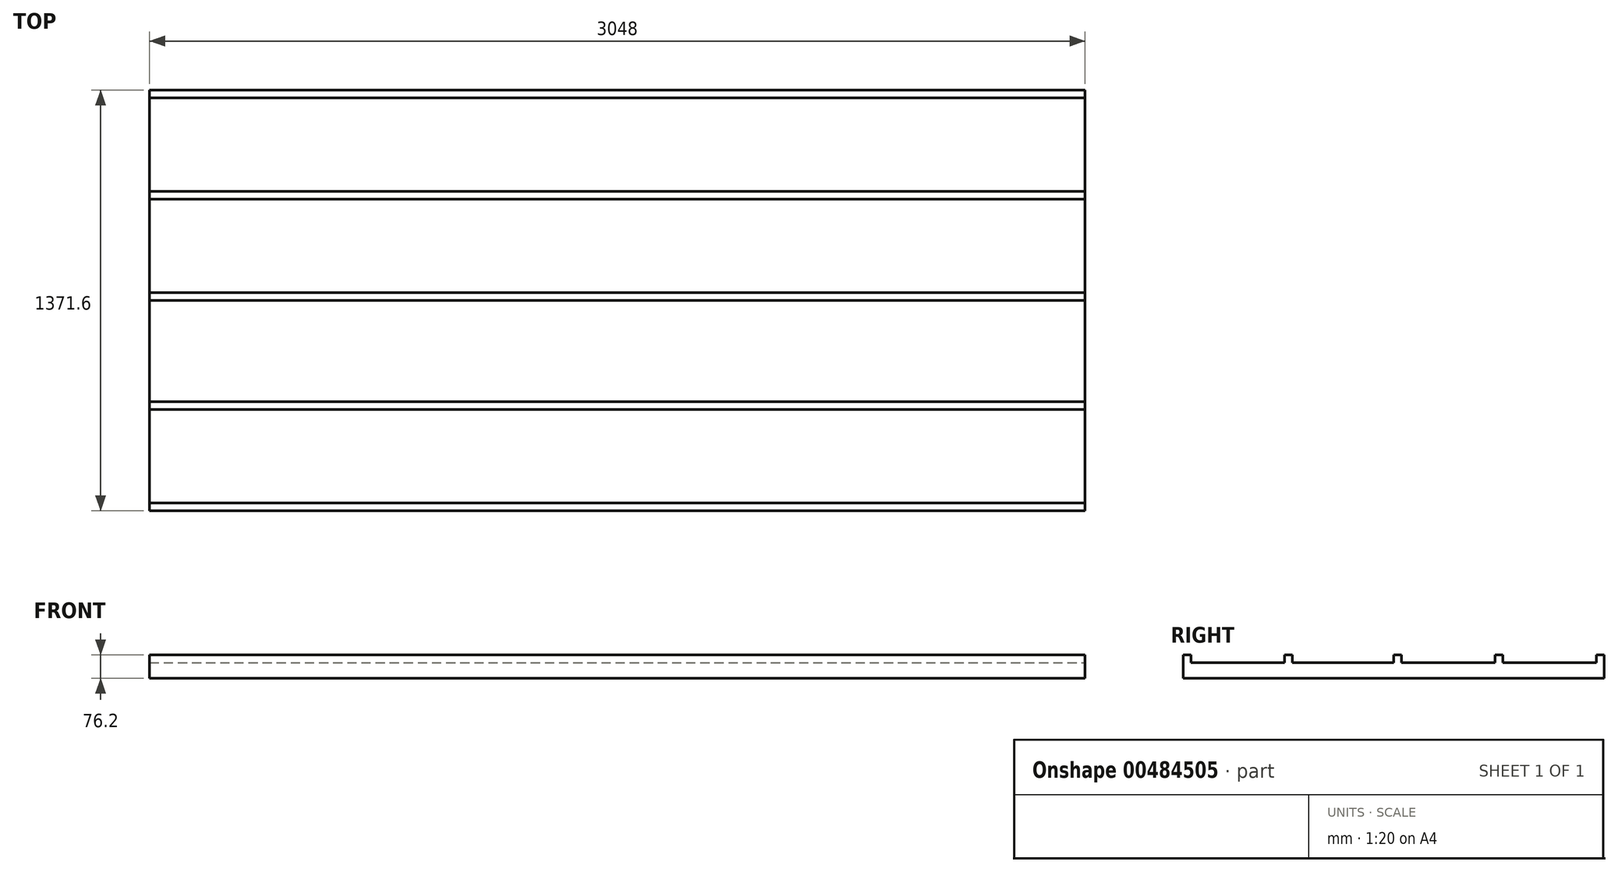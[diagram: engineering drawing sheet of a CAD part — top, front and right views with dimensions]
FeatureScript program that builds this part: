
annotation { "Feature Type Name" : "Feature", "Feature Type Description" : "" }
export const myFeature = defineFeature(function(context is Context, id is Id, definition is map)
    precondition{}
    {
        {
            var Q0;
            Q0=qCreatedBy(makeId("Top.planeOp"),FACE);
            var sketch = newSketch(context, id + "F0", { "sketchPlane" : qUnion([Q0])});
            skLineSegment(sketch, "E0.bottom", {"start": v(-1025.36, 762) * mm, "end": v(2022.64, 762) * mm});
            skLineSegment(sketch, "E0.top", {"start": v(-1025.36, -609.6) * mm, "end": v(2022.64, -609.6) * mm});
            skLineSegment(sketch, "E0.left", {"start": v(-1025.36, 762) * mm, "end": v(-1025.36, -609.6) * mm});
            skLineSegment(sketch, "E0.right", {"start": v(2022.64, 762) * mm, "end": v(2022.64, -609.6) * mm});
            skSolve(sketch);
        }
        {
            var Q0;
            Q0 = qSketchRegion(id + "F0", true);
            var Q1;
            Q1=makeQuery(id+"F0.imprint","IMPRINT",FACE,{"disambiguationData":[TD([[makeQuery(id+"F0.imprint","IMPRINT",EDGE,{"derivedFrom":sQuery(id+"F0.wireOp",EDGE,"E0.bottom")}),-1.0]])]});
            extrude(context, id + "F1", {"entities" : qUnion([Q0, Q1]), "depth" : 50.8 * mm});
        }
        {
            var Q0;
            Q0=makeQuery(id+"F1.opExtrude","CAP_FACE",FACE,{"disambiguationData":[OSD([sQuery(id+"F0.wireOp",EDGE,"E0.bottom"),sQuery(id+"F0.wireOp",EDGE,"E0.top"),sQuery(id+"F0.wireOp",EDGE,"E0.left"),sQuery(id+"F0.wireOp",EDGE,"E0.right")])],"isStart":false});
            var sketch = newSketch(context, id + "F2", { "sketchPlane" : qUnion([Q0])});
            skLineSegment(sketch, "E1.bottom", {"start": v(-1025.36, 762) * mm, "end": v(2022.64, 762) * mm});
            skLineSegment(sketch, "E1.top", {"start": v(-1025.36, 736.6) * mm, "end": v(2022.64, 736.6) * mm});
            skLineSegment(sketch, "E1.left", {"start": v(-1025.36, 762) * mm, "end": v(-1025.36, 736.6) * mm});
            skLineSegment(sketch, "E1.right", {"start": v(2022.64, 762) * mm, "end": v(2022.64, 736.6) * mm});
            skLineSegment(sketch, "E2.bottom", {"start": v(-1025.36, -609.6) * mm, "end": v(2022.64, -609.6) * mm});
            skLineSegment(sketch, "E2.top", {"start": v(-1025.36, -584.2) * mm, "end": v(2022.64, -584.2) * mm});
            skLineSegment(sketch, "E2.left", {"start": v(-1025.36, -609.6) * mm, "end": v(-1025.36, -584.2) * mm});
            skLineSegment(sketch, "E2.right", {"start": v(2022.64, -609.6) * mm, "end": v(2022.64, -584.2) * mm});
            skLineSegment(sketch, "E3.bottom", {"start": v(-1025.36, -279.4) * mm, "end": v(2022.64, -279.4) * mm});
            skLineSegment(sketch, "E3.top", {"start": v(-1025.36, -254) * mm, "end": v(2022.64, -254) * mm});
            skLineSegment(sketch, "E3.left", {"start": v(-1025.36, -279.4) * mm, "end": v(-1025.36, -254) * mm});
            skLineSegment(sketch, "E3.right", {"start": v(2022.64, -279.4) * mm, "end": v(2022.64, -254) * mm});
            skLineSegment(sketch, "E4.left", {"start": v(-1025.36, -25.4) * mm, "end": v(-1025.36, 0) * mm});
            skLineSegment(sketch, "E4.right", {"start": v(2022.64, -25.4) * mm, "end": v(2022.64, 0) * mm});
            skLineSegment(sketch, "E5.bottom", {"start": v(-1025.36, 406.4) * mm, "end": v(2022.64, 406.4) * mm});
            skLineSegment(sketch, "E5.top", {"start": v(-1025.36, 431.8) * mm, "end": v(2022.64, 431.8) * mm});
            skLineSegment(sketch, "E5.left", {"start": v(-1025.36, 406.4) * mm, "end": v(-1025.36, 431.8) * mm});
            skLineSegment(sketch, "E5.right", {"start": v(2022.64, 406.4) * mm, "end": v(2022.64, 431.8) * mm});
            skLineSegment(sketch, "E6.bottom", {"start": v(-1025.36, 101.6) * mm, "end": v(2022.64, 101.6) * mm});
            skLineSegment(sketch, "E6.top", {"start": v(-1025.36, 76.2) * mm, "end": v(2022.64, 76.2) * mm});
            skLineSegment(sketch, "E6.left", {"start": v(-1025.36, 101.6) * mm, "end": v(-1025.36, 76.2) * mm});
            skLineSegment(sketch, "E6.right", {"start": v(2022.64, 101.6) * mm, "end": v(2022.64, 76.2) * mm});
            skSolve(sketch);
        }
        {
            var Q0;
            Q0=makeQuery(id+"F2.imprint","IMPRINT",FACE,{"disambiguationData":[TD([[makeQuery(id+"F2.imprint","IMPRINT",EDGE,{"derivedFrom":sQuery(id+"F2.wireOp",EDGE,"E1.bottom")}),-1.0]])]});
            var Q1;
            Q1=makeQuery(id+"F2.imprint","IMPRINT",FACE,{"disambiguationData":[TD([[makeQuery(id+"F2.imprint","IMPRINT",EDGE,{"derivedFrom":sQuery(id+"F2.wireOp",EDGE,"E5.bottom")}),1.0]])]});
            var Q2;
            Q2=makeQuery(id+"F2.imprint","IMPRINT",FACE,{"disambiguationData":[TD([[makeQuery(id+"F2.imprint","IMPRINT",EDGE,{"derivedFrom":sQuery(id+"F2.wireOp",EDGE,"E6.bottom")}),-1.0]])]});
            var Q3;
            Q3=makeQuery(id+"F2.imprint","IMPRINT",FACE,{"disambiguationData":[TD([[makeQuery(id+"F2.imprint","IMPRINT",EDGE,{"derivedFrom":sQuery(id+"F2.wireOp",EDGE,"E3.bottom")}),1.0]])]});
            var Q4;
            Q4=makeQuery(id+"F2.imprint","IMPRINT",FACE,{"disambiguationData":[TD([[makeQuery(id+"F2.imprint","IMPRINT",EDGE,{"derivedFrom":sQuery(id+"F2.wireOp",EDGE,"E2.bottom")}),1.0]])]});
            extrude(context, id + "F3", {"entities" : qUnion([Q0, Q1, Q2, Q3, Q4]), "operationType" : NewBodyOperationType.ADD, "depth" : 25.4 * mm});
        }
    });
